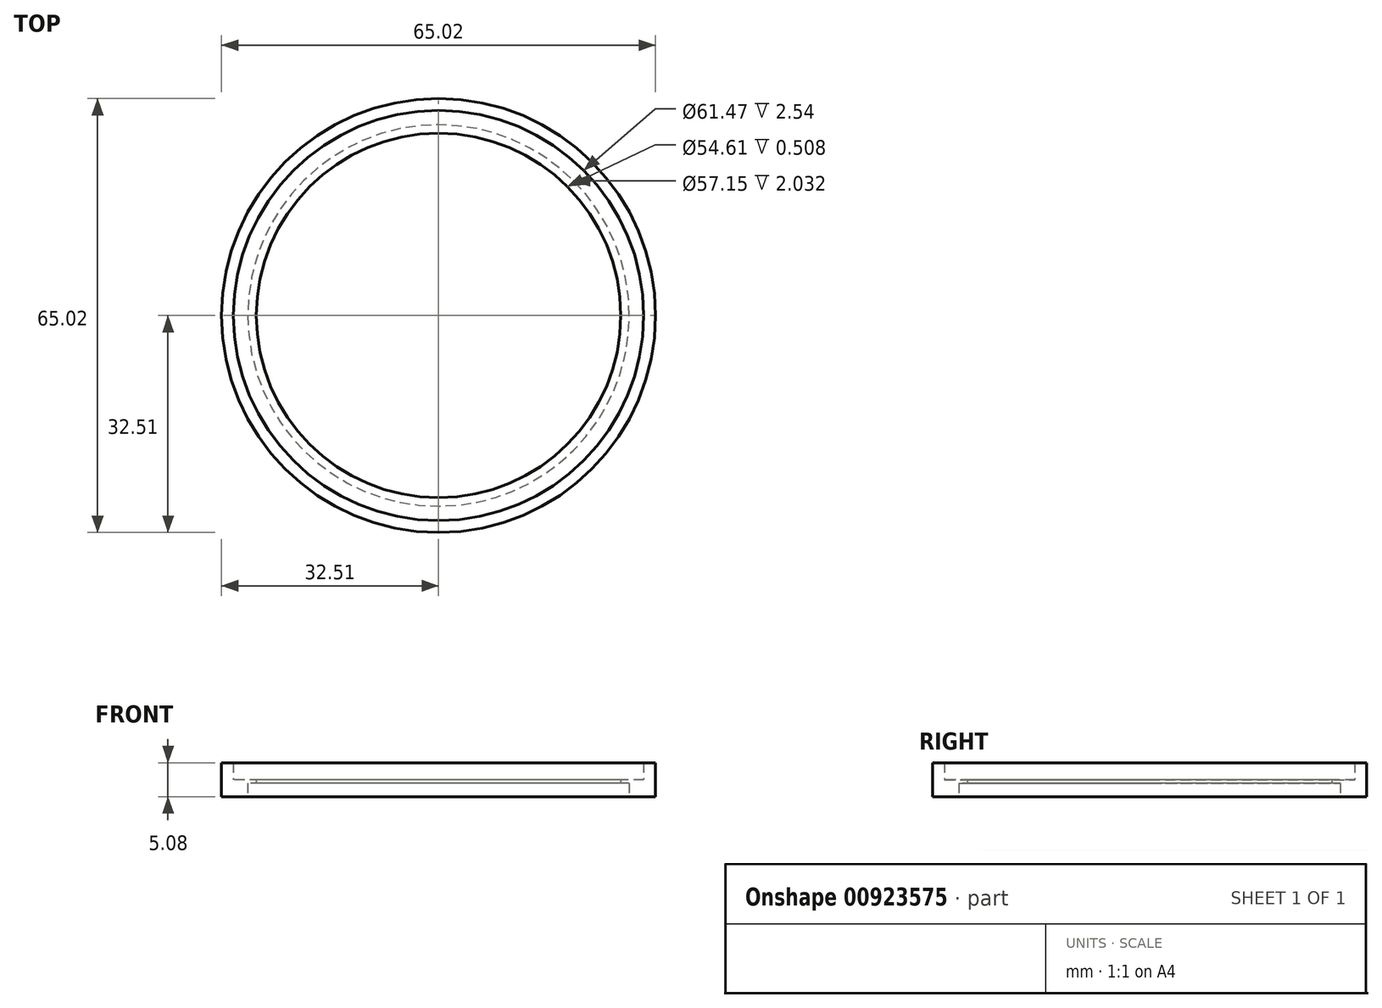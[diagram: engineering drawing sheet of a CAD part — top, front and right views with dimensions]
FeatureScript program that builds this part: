
annotation { "Feature Type Name" : "Feature", "Feature Type Description" : "" }
export const myFeature = defineFeature(function(context is Context, id is Id, definition is map)
    precondition{}
    {
        {
            var Q0;
            Q0=qCreatedBy(makeId("Top.planeOp"),FACE);
            var sketch = newSketch(context, id + "F0", { "sketchPlane" : qUnion([Q0])});
            skCircle(sketch, "E0", {"center": v(0, 0) * mm, "radius": 30.73 * mm});
            skCircle(sketch, "E1", {"center": v(0, 0) * mm, "radius": 32.51 * mm});
            skCircle(sketch, "E2", {"center": v(0, 0) * mm, "radius": 27.3 * mm});
            skSolve(sketch);
        }
        {
            var Q0;
            Q0=makeQuery(id+"F0.imprint","IMPRINT",FACE,{"disambiguationData":[TD([[makeQuery(id+"F0.imprint","IMPRINT",EDGE,{"derivedFrom":sQuery(id+"F0.wireOp",EDGE,"E0")}),-1.0]])]});
            extrude(context, id + "F1", {"entities" : qUnion([Q0]), "depth" : 5.08 * mm, "offsetDistance" : 25.4 * mm});
        }
        {
            var Q0;
            Q0=makeQuery(id+"F0.imprint","IMPRINT",FACE,{"disambiguationData":[TD([[makeQuery(id+"F0.imprint","IMPRINT",EDGE,{"derivedFrom":sQuery(id+"F0.wireOp",EDGE,"E0")}),1.0]])]});
            extrude(context, id + "F2", {"entities" : qUnion([Q0]), "operationType" : NewBodyOperationType.ADD, "depth" : 2.54 * mm, "offsetDistance" : 25.4 * mm});
        }
        {
            var Q0;
            Q0=qCreatedBy(makeId("Top.planeOp"),FACE);
            var sketch = newSketch(context, id + "F3", { "sketchPlane" : qUnion([Q0])});
            skCircle(sketch, "E3", {"center": v(0, 0) * mm, "radius": 28.57 * mm});
            skCircle(sketch, "E4", {"center": v(0, 0) * mm, "radius": 27.3 * mm});
            skSolve(sketch);
        }
        {
            var Q0;
            Q0=makeQuery(id+"F3.imprint","IMPRINT",FACE,{"disambiguationData":[TD([[makeQuery(id+"F3.imprint","IMPRINT",EDGE,{"derivedFrom":sQuery(id+"F3.wireOp",EDGE,"E3")}),1.0]])]});
            extrude(context, id + "F4", {"entities" : qUnion([Q0]), "operationType" : NewBodyOperationType.REMOVE, "depth" : 2.03 * mm, "offsetDistance" : 25.4 * mm});
        }
    });
